# Revit family: Artemide_Discovery_Suspended
name_source: partatom
category: Lighting Fixtures
revit_build: Autodesk Revit 2018 (Build: 20190510_1515(x64)
units: mm (PartAtom-declared; Revit-internal decimal feet)

## family parameters
Always vertical = Yes
Cut with Voids When Loaded = No
Light Source = Yes
Part Type = Normal
Room Calculation Point = No
Round Connector Dimension = Use Diameter
Shared = No
Work Plane-Based = Yes

## types (6) — shared parameters
6 Monthly = -
Air Handling = -
Annually = -
Application Environment = Internal
Beam Angle Longditudinal Axis  = 0.00°
Beam Angle Transverse Axis  = 0.00°
Bespoke Timeframe = -
CE Approval = Y
Cable Material = -
Color Filter = 16777215
Colour Rendering Index = 90
Colour Temperature = 3000
Column = -
Control Gear Location = -
Control Gear Required = -
Control Gear Type = -
Daily = -
Daylight Sensor = -
Default Elevation = 1219 mm
Diameter_Lamp = 702 mm
Diffuser Finish = -
Diffuser Material  = -
Diffusing screen = -
Dimming Lamp Color Temperature Shift = <None>
ENEC Certification of European conformity = Y
Earth Point  = -
Efficiency = 52
Emergency = N
Emergency Lighting Battery = -
Emit Shape Visible in Rendering = No
Emit from Circle Diameter = 610 mm
End Caps/Transition Caps/Joints = -
Environmental Product Declaration = -
Expected Life = -
Face Shape = Circular
Features = -
Fire Rated = -
Fire Shroud = -
Fixing Material = -
Fixings = Y
Gasket Material = -
Green Guide for Specification = -
Gross Weight = 3.68
Hazardous Area Category = -
Hazardous Area Protection Type = -
Housing Material = Alluminum
IES Files  = https://www.artemide.com
IK Rating = -
IP Rating = IP20
IfcExportAs = IfcLightFixtureType
IfcExportType = NOT DEFINED
Infills = -
Initial Lumens = 2298
Input Lumens Direct light = 648
Integral Emergency Lighting Battery Type = -
Integral Fuse or Circuit Protection  = -
Intended Market = Unset
International Type Code = -
LED lifetime = 50000
Lamp Cap = LED Integrated
Lamp Holder Material = -
Lamp Included = Y
Lamp Replacement Interval = -
Lamp Survival Factor = -
Life Cycle Analysis = -
Light Fixture Mounting Type = Suspended
Light Output Pattern = -
Location of Manufacturer = -
Louvre/Lens = -
Luminaire Cleaning Interval  = -
Luminaire Type = Downlight
M_Diffuser = Artemide_Glass_LightBulb
M_Fixings = Artemide_Aluminum_Anodized
Maintenance Required: 0-300hrs  = -
Maintenance Required: 1001-2000hrs  = -
Maintenance Required: 2001-4000hrs  = -
Maintenance Required: 301-600hrs  = -
Maintenance Required: 4001-8000hrs  = -
Maintenance Required: 601-1000hrs = -
Maintenance Required: 8001-12000hrs  = -
Manufacturer = Artemide
Manufacturer Website = https://www.artemide.com
Material Ingredient Reporting = -
Max Height from ceiling = 1650 mm
Monthly = -
Motion Detector = -
Motion Sensor = -
Number of Primary Lamps = 7
Output Lumens Direct light = 2298
Overall Height = 17
Overall Length = 700
Photocell = -
Power Supply Kit = -
Primary Lamp Type = LED
Product Literature = https://www.artemide.com
Product Range = Discovery
Quarterly = -
Radius_Diffuser = 335 mm  [stored 1.09908 ft]
Radius_ExternalLamp = 351 mm
Rated Lamp Life = 50000
Reflector Finish = -
Reflector Material = Technopolymer
Responsible Extraction of Materials = -
Responsible Sourcing of Materials = -
Secondary Lamp = N
Secondary Lamp Cap = -
Secondary Lamp Included = -
Secondary Lamp International Type Code = -
Service life  = -
Standards = -
Suitable for Dimming  = Y
Suitable for Motion Detector Control = N
Suitable for Photocell Control = -
Testing method = -
Tilt Angle = 90.00°
Trim Colour  = -
Trim Finish = -
Trim Material = -
URL to Energy Technology List = -
URL to O&M Manual = https://www.artemide.com
Uniclass 2015 = Pr_70_70_48
Unified Glare Rating  = -
Voltage = -
Warranty ID = https://cloud.artemide.com
Wattage  = 46
Weekly = -
zero-valued in all types: Access Clearance Bottom, Access Clearance Front, Access Clearance Left, Access Clearance Rear, Access Clearance Right, Access Clearance Top, Ambient Temperature                            , Basis of lifetime lumen depreciation  , Basis of lifetime luminaire failures       , Control Gear Standby Power , Current , Cut Out Length, Cut Out Width, Downward Component, Drive Current                                         , Duration of Integral Emergency Lighting , Embodied Carbon , Emergency Charging Power      , Emergency light output percentage, External Control Line Voltage, Face Length, Face Width, Fire Rated Temperature, Fire Rating Duration, Frequency , Input Lumens Indirect light, LED Initial Colour Variation                     , LED Maintained Colour Variation        , Luminaire Maintenance Factor, Luminance at 65deg Angle, Maximum Operating Temperature, Minimum Operating Temperature, Number of Poles, Number of Secondary Lamps, Output Lumens Indirect light, Overall Light Output Ratio, Overall Width, Power Factor, Secondary Lamp Colour Rendering Index, Secondary Lamp Colour Temperature, Secondary Lamp Efficacy, Secondary Lamp Initial Lumens , Secondary Lamp Voltage, Secondary Rated Lamp Life, Shipping Weight, Supply Phase, Total Light Output , Total Power, Upward Component 

## per-type parameters (varying)
| type | Housing Colour  | Housing Finish  | M_Housing | Photometric Web File | Product Model Number | Suitable Dimmer Type |
| Discovery _Suspended _Satinized Aluminum_1999110A | Aluminum | Satinized | Artemide_Aluminum_Satinized | 1999010A.IES | 1999110A | Push |
| Discovery _Suspended _Satinized Aluminum_APPCompatible_1999110APP | Aluminum | Satinized | Artemide_Aluminum_Satinized | 1999110APP.IES | 1999110APP | Push & APP |
| Discovery _Suspended _Black_1999130A | Black | Painted | Artemide_Aluminum_Black | 1999130A.IES | 1999130A | Push |
| Discovery _Suspended _Black_APPCompatible_1999130APP | Black | Painted | Artemide_Aluminum_Black | 1999130APP.IES | 1999130APP | Push & APP |
| Discovery _Suspended _Bronze_1999160A | Bronze | Painted | Artemide_Aluminum_Bronze | 1999160A.IES | 1999160A | Push |
| Discovery _Suspended _Bronze_APPCompatible_1999160APP | Bronze | Painted | Artemide_Aluminum_Bronze | 1999160APP.IES | 1999160APP | Push & APP |

note: [stored X ft] marks values corroborated as IEEE doubles in the binary element streams (Revit-internal decimal feet)

## geometry (parser evidence)
native form markers: Blend x2, Sweep x5
no freeform markers — native parametric forms only
